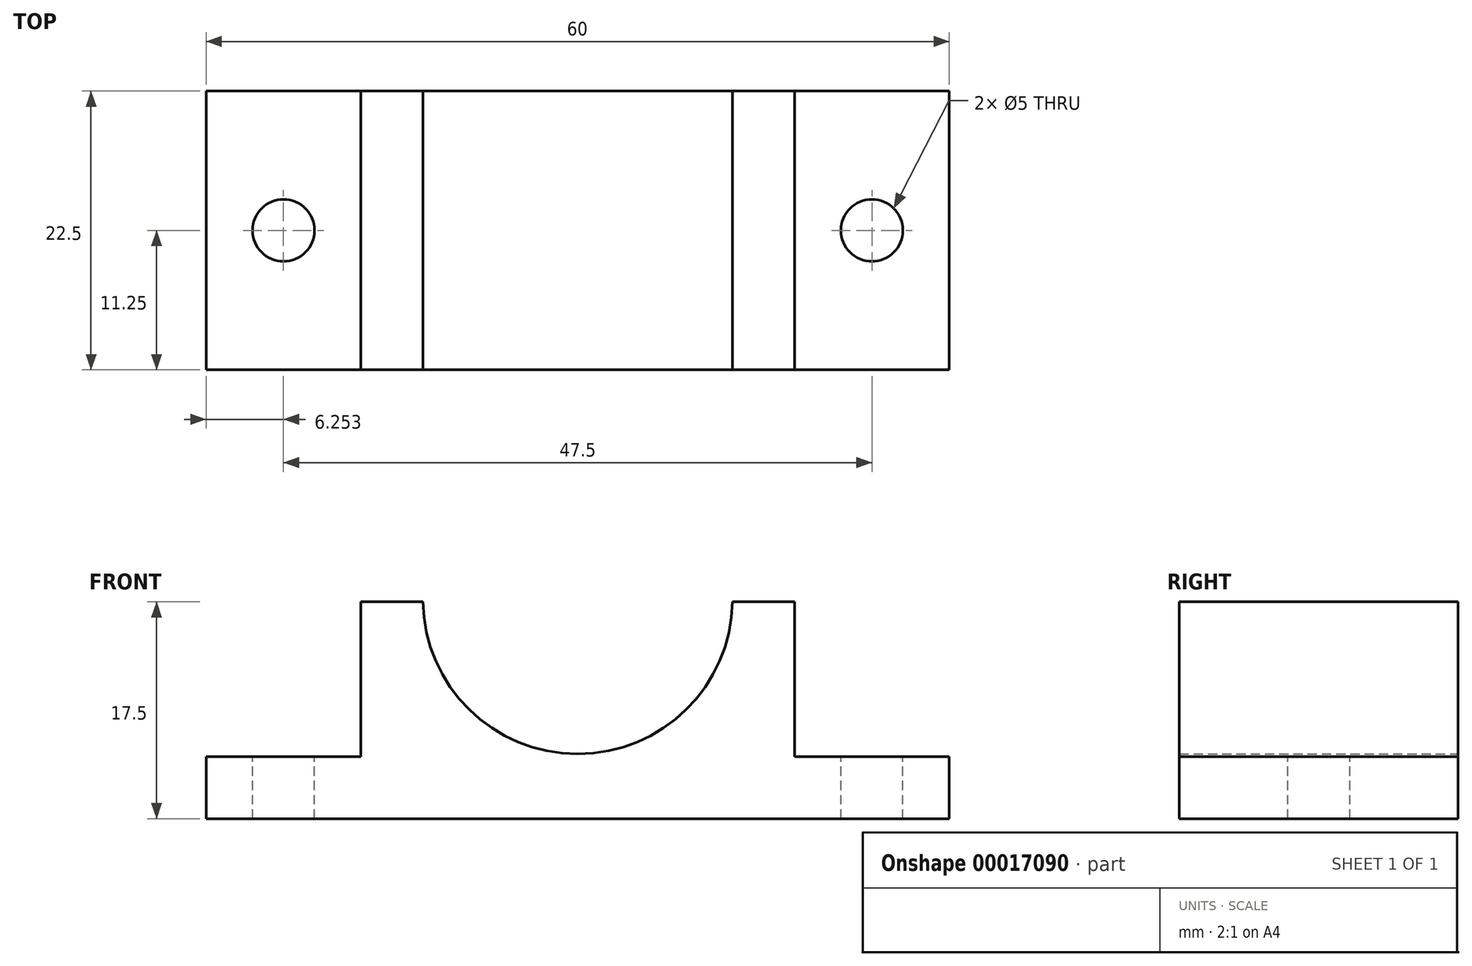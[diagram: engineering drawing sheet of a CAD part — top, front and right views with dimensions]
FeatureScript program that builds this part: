
annotation { "Feature Type Name" : "Feature", "Feature Type Description" : "" }
export const myFeature = defineFeature(function(context is Context, id is Id, definition is map)
    precondition{}
    {
        {
            var Q0;
            Q0=qCreatedBy(makeId("Front.planeOp"),FACE);
            var sketch = newSketch(context, id + "F0", { "sketchPlane" : qUnion([Q0])});
            skLineSegment(sketch, "E0", {"start": v(-31.89, -8.19) * mm, "end": v(28.11, -8.19) * mm});
            skLineSegment(sketch, "E1", {"start": v(-31.89, -8.19) * mm, "end": v(-31.89, -3.19) * mm});
            skLineSegment(sketch, "E2", {"start": v(-31.89, -3.19) * mm, "end": v(-19.39, -3.19) * mm});
            skLineSegment(sketch, "E3", {"start": v(-19.39, -3.19) * mm, "end": v(-19.39, 9.31) * mm});
            skLineSegment(sketch, "E4", {"start": v(15.61, 9.31) * mm, "end": v(15.61, -3.19) * mm});
            skLineSegment(sketch, "E5", {"start": v(15.61, -3.19) * mm, "end": v(28.11, -3.19) * mm});
            skLineSegment(sketch, "E6", {"start": v(28.11, -3.19) * mm, "end": v(28.11, -8.19) * mm});
            skLineSegment(sketch, "E7", {"start": v(-19.39, 9.31) * mm, "end": v(-14.39, 9.31) * mm});
            skLineSegment(sketch, "E8", {"start": v(10.6, 9.31) * mm, "end": v(15.61, 9.31) * mm});
            skArc(sketch, "E9", {"start": v(-14.39, 9.31) * mm, "mid": v(-1.89, -2.97) * mm, "end": v(10.6, 9.31) * mm});
            skSolve(sketch);
        }
        {
            var Q0;
            Q0=makeQuery(id+"F0.imprint","IMPRINT",FACE,{"disambiguationData":[TD([[makeQuery(id+"F0.imprint","IMPRINT",EDGE,{"derivedFrom":sQuery(id+"F0.wireOp",EDGE,"E0")}),1.0]])]});
            extrude(context, id + "F1", {"entities" : qUnion([Q0]), "depth" : 22.5 * mm});
        }
        {
            var Q0;
            Q0=makeQuery(id+"F1.opExtrude","SWEPT_FACE",FACE,{"disambiguationData":[OSD([sQuery(id+"F0.wireOp",EDGE,"E5")])]});
            var sketch = newSketch(context, id + "F2", { "sketchPlane" : qUnion([Q0])});
            skCircle(sketch, "E10", {"center": v(21.86, -11.25) * mm, "radius": 2.5 * mm});
            skSolve(sketch);
        }
        {
            var Q0;
            Q0=makeQuery(id+"F1.opExtrude","SWEPT_FACE",FACE,{"disambiguationData":[OSD([sQuery(id+"F0.wireOp",EDGE,"E2")])]});
            var sketch = newSketch(context, id + "F3", { "sketchPlane" : qUnion([Q0])});
            skCircle(sketch, "E11", {"center": v(-25.64, -11.25) * mm, "radius": 2.5 * mm});
            skSolve(sketch);
        }
        {
            var Q0;
            Q0 = qSketchRegion(id + "F3", true);
            var Q1;
            Q1 = qSketchRegion(id + "F2", true);
            extrude(context, id + "F4", {"entities" : qUnion([Q0, Q1]), "operationType" : NewBodyOperationType.REMOVE, "endBound" : BoundingType.THROUGH_ALL, "oppositeDirection" : true, "depth" : 25 * mm});
        }
        {
            var Q0;
            Q0=makeQuery(id+"F2.imprint","IMPRINT",FACE,{"disambiguationData":[TD([[makeQuery(id+"F2.imprint","IMPRINT",EDGE,{"derivedFrom":sQuery(id+"F2.wireOp",EDGE,"E10")}),1.0]])]});
            extrude(context, id + "F5", {"entities" : qUnion([Q0]), "operationType" : NewBodyOperationType.REMOVE, "endBound" : BoundingType.THROUGH_ALL, "oppositeDirection" : true, "depth" : 25 * mm});
        }
    });
